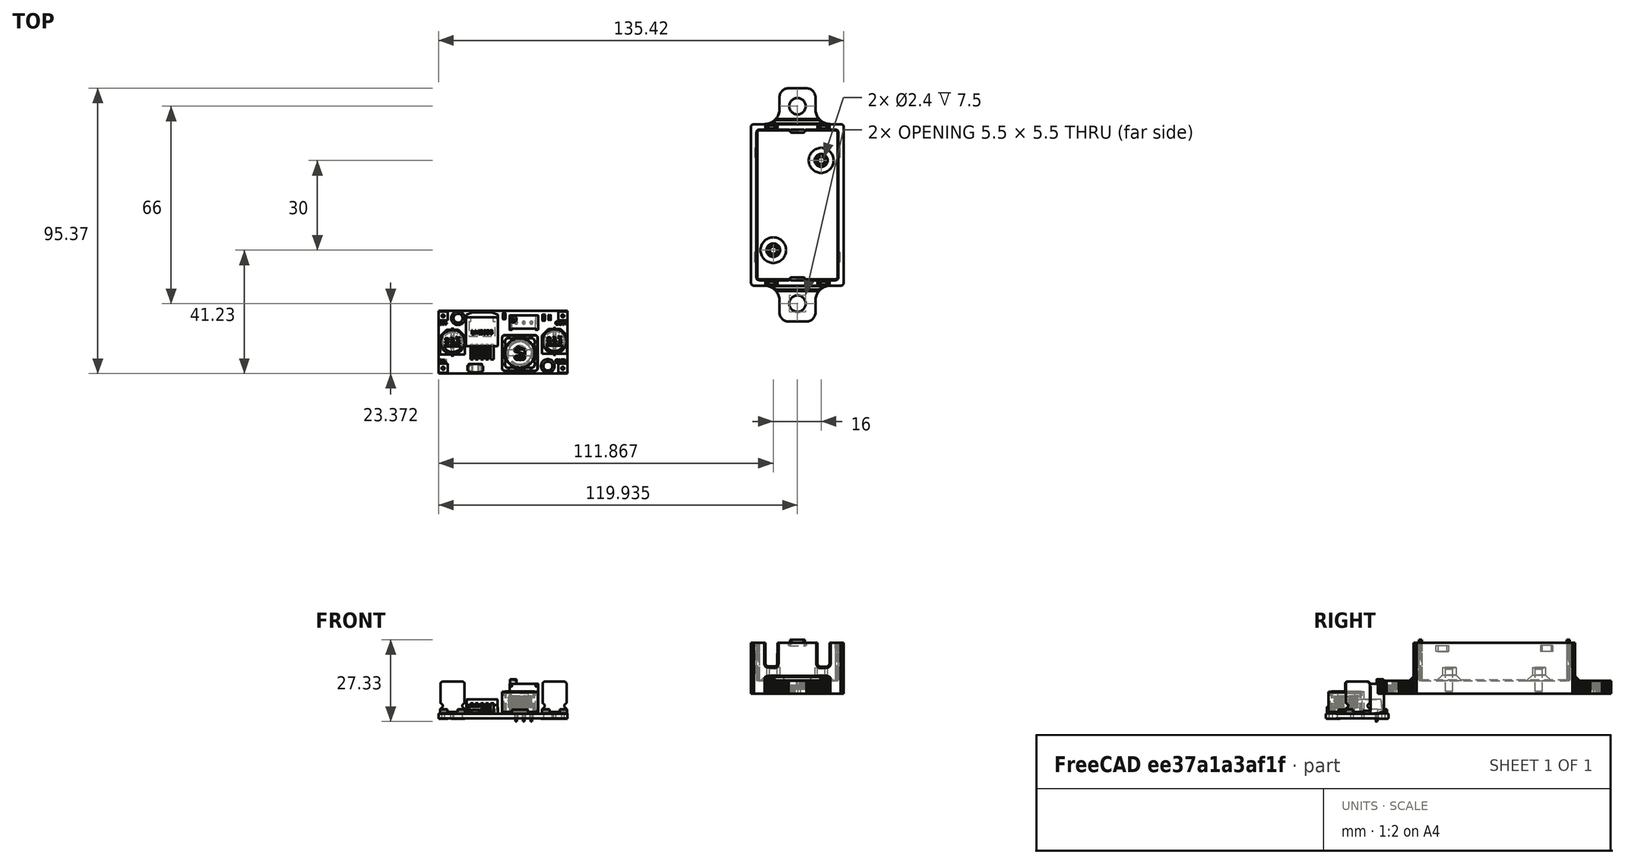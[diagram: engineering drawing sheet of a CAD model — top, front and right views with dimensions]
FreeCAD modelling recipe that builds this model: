
FCSTD DOCUMENT  (FreeCAD 1.1R44348 (Git))
Label: BuckConverterLM2956
License: All rights reserved
LicenseURL: https://en.wikipedia.org/wiki/All_rights_reserved
objects: Part::Feature×14, Sketcher::SketchObject×4, Mesh::Feature×2, App::Point×2, PartDesign::Pocket×2, PartDesign::Pad×2, PartDesign::Chamfer×2, Part::Refine×1, Part::FeaturePython×1, Part::Extrusion×1, Part::MultiFuse×1, PartDesign::FeatureBase×1, App::Part×1, PartDesign::SubShapeBinder×1, PartDesign::Body×1
note: 48 computed .brp shape members not serialized (recipe doc carries the construction recipe); baked Part::Feature solids carry a one-line shape summary decoded from their .brp

FEATURE [Mesh::Feature] Buck_Converter_Box___base  label="Buck_Converter_Box - base"
FEATURE [Part::Feature] Buck_Converter_Box___base001
  shape: bbox 31 x 78 x 15 mm, 13338 faces, 0 solids (baked)
FEATURE [Part::Refine] Buck_Converter_Box___base002
  Source = -> Buck_Converter_Box___base001
FEATURE [Part::Feature] Buck_Converter_Box___base002_solid  label="Buck_Converter_Box___base002 (Solid)"
  shape: bbox 31 x 78 x 15 mm, 9872 faces (baked)
FEATURE [Part::FeaturePython] Facebinder  # WARN: FeaturePython — macro-defined, semantics opaque (R4)
  Area = 1927.48
  Extrusion = 0
  Faces = -> [Buck_Converter_Box___base002_solid]
  RemoveSplitter = false
  Sew = false
FEATURE [Part::Extrusion] Extrude
  Base = -> Facebinder
  Dir = (0,0,-1)
  DirMode = 2
  FaceMakerClass = Part::FaceMakerBullseye
  FaceMakerMode = 3
  LengthFwd = 3
  LengthRev = 0
  Solid = false
  Symmetric = false
FEATURE [Part::MultiFuse] Fusion
  Refine = true
  Shapes = -> [Extrude,Buck_Converter_Box___base002_solid]
FEATURE [App::Point] Origin001
  Role = Origin
FEATURE [PartDesign::FeatureBase] BaseFeature
  BaseFeature = -> Fusion
  Suppressed = false
FEATURE [Sketcher::SketchObject] Sketch
  ArcFitTolerance = 1e-06
  AttachmentSupport = -> [BaseFeature]
  ExternalTypes = [0,0]
  FullyConstrained = false
  MakeInternals = false
  MapMode = 5
  Placement = pos=(0,0,6) rot=(0,0,1;0rad)
  sketch-geometry (2):
    g0: Circle CenterX=72.4135 CenterY=65.2773 CenterZ=0 NormalX=0 NormalY=0 NormalZ=1 AngleXU=0 Radius=4.12718
    g1: Circle CenterX=84.7195 CenterY=33.1699 CenterZ=0 NormalX=0 NormalY=0 NormalZ=1 AngleXU=0 Radius=4.19336
FEATURE [PartDesign::Pocket] Pocket
  BaseFeature = -> BaseFeature
  Direction = (0,0,-1)
  Length = 5
  Length2 = 5
  Profile = -> Sketch
  ReferenceAxis = -> Sketch [N_Axis]
  Refine = true
  SideType = 0
  Suppressed = false
  Type = 3
  Type2 = 0
  UpToFace = -> BaseFeature [Face427]
FEATURE [Part::Feature] Part__Feature  label="Board v5"
  Placement = pos=(0,-9.73272,-11.3327) rot=(1,0,0;1.5708rad)
  shape: bbox 43 x 21 x 1.7 mm, 395 faces (baked)
FEATURE [Part::Feature] Part__Feature001  label="Trimpot 3296W v1"
  Placement = pos=(-14.54,7.27228,-9.73272) rot=(0,0,1;3.14159rad)
  shape: bbox 9.53 x 4.83 x 14.15 mm, 96 faces (baked)
FEATURE [Part::Feature] Part__Feature002  label="CDRH127_470M v1"
  Placement = pos=(-15.855,-2.88272,-9.74272) rot=(0,0,-1;1.5708rad)
  shape: bbox 12.31 x 12.77 x 7.426 mm, 258 faces, 6 solids (baked)
FEATURE [Part::Feature] Part__Feature003  label="CAPSMD220-35 v1"
  Placement = pos=(-4.26006,1.02456,-9.73272) rot=(0,0,1;1.5708rad)
  shape: bbox 8.659 x 9 x 39.03 mm, 183 faces (baked)
FEATURE [Part::Feature] Part__Feature004  label="CAPSMD100-50 v1"
  Placement = pos=(-38.35,0.747284,-9.73272) rot=(0,0,1;1.5708rad)
  shape: bbox 8.659 x 9 x 39.03 mm, 169 faces (baked)
FEATURE [Part::Feature] Part__Feature005  label="TO-263BA v2"
  Placement = pos=(-31.9,-3.43272,-9.73272) rot=(0,0,1;0rad)
  shape: bbox 10.65 x 15.86 x 4.815 mm, 299 faces, 7 solids (baked)
FEATURE [Part::Feature] Part__Feature006  label="DO-214AC-DIOM5127X23N v1"
  Placement = pos=(-32.735,-7.98272,-9.73272) rot=(0,0,1;0rad)
  shape: bbox 5.305 x 2.805 x 2.305 mm, 82 faces, 3 solids (baked)
FEATURE [Part::Feature] Part__Feature007  label="Resistor 0603 v1"
  Placement = pos=(-19.95,10.2673,-9.73272) rot=(0.57735,-0.57735,-0.57735;2.0944rad)
  shape: bbox 0.8134 x 2.113 x 0.6107 mm, 158 faces, 9 solids (baked)
FEATURE [Part::Feature] Part__Feature008  label="Resistor 0603 v1 (1)"
  Placement = pos=(-6.75,9.76728,-9.73272) rot=(0.57735,-0.57735,-0.57735;2.0944rad)
  shape: bbox 0.8134 x 2.113 x 0.6107 mm, 158 faces, 9 solids (baked)
FEATURE [Part::Feature] Part__Feature009  label="CAP0603 v1"
  Placement = pos=(-21.085,5.98228,-9.73272) rot=(0,0,-1;1.5708rad)
  shape: bbox 0.819 x 1.619 x 0.319 mm, 42 faces, 0 solids (baked)
FEATURE [Part::Feature] Part__Feature010  label="LED Blue SMD 0603 W\X\FCrth 150060BS55040 v1"
  Placement = pos=(-5.89,8.97728,-9.73272) rot=(0,0,-1;1.5708rad)
  shape: bbox 0.8 x 1.616 x 0.4 mm, 133 faces (baked)
FEATURE [Part::Feature] Part__Feature011  label="CAP0603 v1 (1)"
  Placement = pos=(-35.385,-5.51772,-9.73272) rot=(0,0,-1;1.5708rad)
  shape: bbox 0.819 x 1.619 x 0.319 mm, 42 faces, 0 solids (baked)
FEATURE [App::Part] LM2596_DC_DC_StepDown_Converter_v1  label="LM2596 DC-DC StepDown Converter v1"
  Group = -> [Part__Feature,Part__Feature001,Part__Feature002,Part__Feature003,Part__Feature004,Part__Feature005,Part__Feature006,Part__Feature007,Part__Feature008,Part__Feature009,Part__Feature010,Part__Feature011]
  Origin = -> Origin002
  Placement = pos=(76.1,25,19) rot=(0,0,1;4.71239rad)
FEATURE [App::Point] Origin003
  Role = Origin
FEATURE [PartDesign::SubShapeBinder] Binder
  BindCopyOnChange = 0
  BindMode = 0
  ClaimChildren = false
  Context = -> Body [Binder.]
  Fuse = false
  MakeFace = true
  OffsetFill = false
  OffsetIntersection = false
  OffsetJoinType = 0
  OffsetOpenResult = false
  PartialLoad = false
  Refine = true
  Relative = true
  Support = -> [LM2596_DC_DC_StepDown_Converter_v1[Part__Feature.Edge1037,Part__Feature.Edge1039,Part__Feature.Edge1040,Part__Feature.Edge1016,Part__Feature.Edge1015,Part__Feature.Edge1013]]
  _Version = 2
FEATURE [Sketcher::SketchObject] Sketch001
  ArcFitTolerance = 1e-06
  AttachmentSupport = -> [Pocket]
  ExternalGeometry = -> [Binder]
  ExternalTypes = [0,0]
  FullyConstrained = false
  MakeInternals = false
  MapMode = 5
  Placement = pos=(0,0,1.2) rot=(0,0,1;0rad)
  sketch-geometry (4):
    g0: Circle CenterX=84.8673 CenterY=61.5 CenterZ=0 NormalX=0 NormalY=0 NormalZ=1 AngleXU=0 Radius=2.16873
    g1: Circle CenterX=68.8673 CenterY=31.5 CenterZ=0 NormalX=0 NormalY=0 NormalZ=1 AngleXU=0 Radius=2.26669
    g2: Circle CenterX=68.8673 CenterY=31.5 CenterZ=0 NormalX=0 NormalY=0 NormalZ=1 AngleXU=0 Radius=1
    g3: Circle CenterX=84.8673 CenterY=61.5 CenterZ=0 NormalX=0 NormalY=0 NormalZ=1 AngleXU=0 Radius=1
  constraints (6):
    c: Coincident(g0,g-3)
    c: Coincident(g1,g-4)
    c: Coincident(g2,g1)
    c: Coincident(g3,g0)
    c: Equal(g2,g3)
    c: Diameter(g3) = 2
FEATURE [PartDesign::Pad] Pad
  BaseFeature = -> Pocket
  Direction = (0,0,1)
  Length = 4.5
  Length2 = 10
  Profile = -> Sketch001
  ReferenceAxis = -> Sketch001 [N_Axis]
  Refine = true
  SideType = 0
  Suppressed = false
  Type = 0
  Type2 = 0
FEATURE [PartDesign::Chamfer] Chamfer
  Angle = 45
  Base = -> Pad [Edge120,Edge47]
  BaseFeature = -> Pad
  ChamferType = 0
  FlipDirection = false
  Refine = true
  Size = 2
  Size2 = 1
  SupportTransform = false
  Suppressed = false
  UseAllEdges = false
FEATURE [Sketcher::SketchObject] Sketch002
  ArcFitTolerance = 1e-06
  AttachmentSupport = -> [Chamfer]
  ExternalTypes = [0]
  FullyConstrained = false
  MakeInternals = false
  MapMode = 5
  Placement = pos=(0,0,1) rot=(0,0,1;0rad)
  sketch-geometry (2):
    g0: Circle CenterX=84.7772 CenterY=33.2485 CenterZ=0 NormalX=0 NormalY=0 NormalZ=1 AngleXU=0 Radius=2.59032
    g1: Circle CenterX=72.5049 CenterY=65.0182 CenterZ=0 NormalX=0 NormalY=0 NormalZ=1 AngleXU=0 Radius=2.25905
FEATURE [PartDesign::Pad] Pad001
  BaseFeature = -> Chamfer
  Direction = (0,0,1)
  Length = 10
  Length2 = 10
  Profile = -> Sketch002
  ReferenceAxis = -> Sketch002 [N_Axis]
  Refine = true
  SideType = 0
  Suppressed = false
  Type = 3
  Type2 = 0
  UpToFace = -> Chamfer [Face1]
FEATURE [Sketcher::SketchObject] Sketch003
  ArcFitTolerance = 1e-06
  AttachmentSupport = -> [Pad001]
  ExternalGeometry = -> [Pad001]
  ExternalTypes = [0,0]
  FullyConstrained = true
  MakeInternals = false
  MapMode = 5
  Placement = pos=(0,0,5.7) rot=(0,0,1;0rad)
  sketch-geometry (2):
    g0: Circle CenterX=84.8673 CenterY=61.5 CenterZ=0 NormalX=0 NormalY=0 NormalZ=1 AngleXU=0 Radius=1.2
    g1: Circle CenterX=68.8673 CenterY=31.5 CenterZ=0 NormalX=0 NormalY=0 NormalZ=1 AngleXU=0 Radius=1.2
  constraints (4):
    c: Coincident(g0,g-4)
    c: Coincident(g1,g-3)
    c: Equal(g1,g0)
    c: Diameter(g0) = 2.4
FEATURE [PartDesign::Pocket] Pocket001
  BaseFeature = -> Pad001
  Direction = (0,0,-1)
  Length = 8
  Length2 = 5
  Profile = -> Sketch003
  ReferenceAxis = -> Sketch003 [N_Axis]
  Refine = true
  SideType = 0
  Suppressed = false
  Type = 0
  Type2 = 0
FEATURE [Mesh::Feature] Buck_Converter_Box___top  label="Buck_Converter_Box - top"
FEATURE [PartDesign::Chamfer] Chamfer001
  Angle = 45
  Base = -> Pocket001 [Edge1773,Edge1774]
  BaseFeature = -> Pocket001
  ChamferType = 0
  FlipDirection = false
  Refine = true
  Size = 0.5
  Size2 = 1
  SupportTransform = false
  Suppressed = false
  UseAllEdges = false
FEATURE [PartDesign::Body] Body  label="Base"
  AllowCompound = true
  BaseFeature = -> Fusion
  Group = -> [BaseFeature,Sketch,Pocket,Binder,Sketch001,Pad,Chamfer,Sketch002,Pad001,Sketch003,Pocket001,Chamfer001]
  Origin = -> Origin
  Tip = -> Chamfer001
